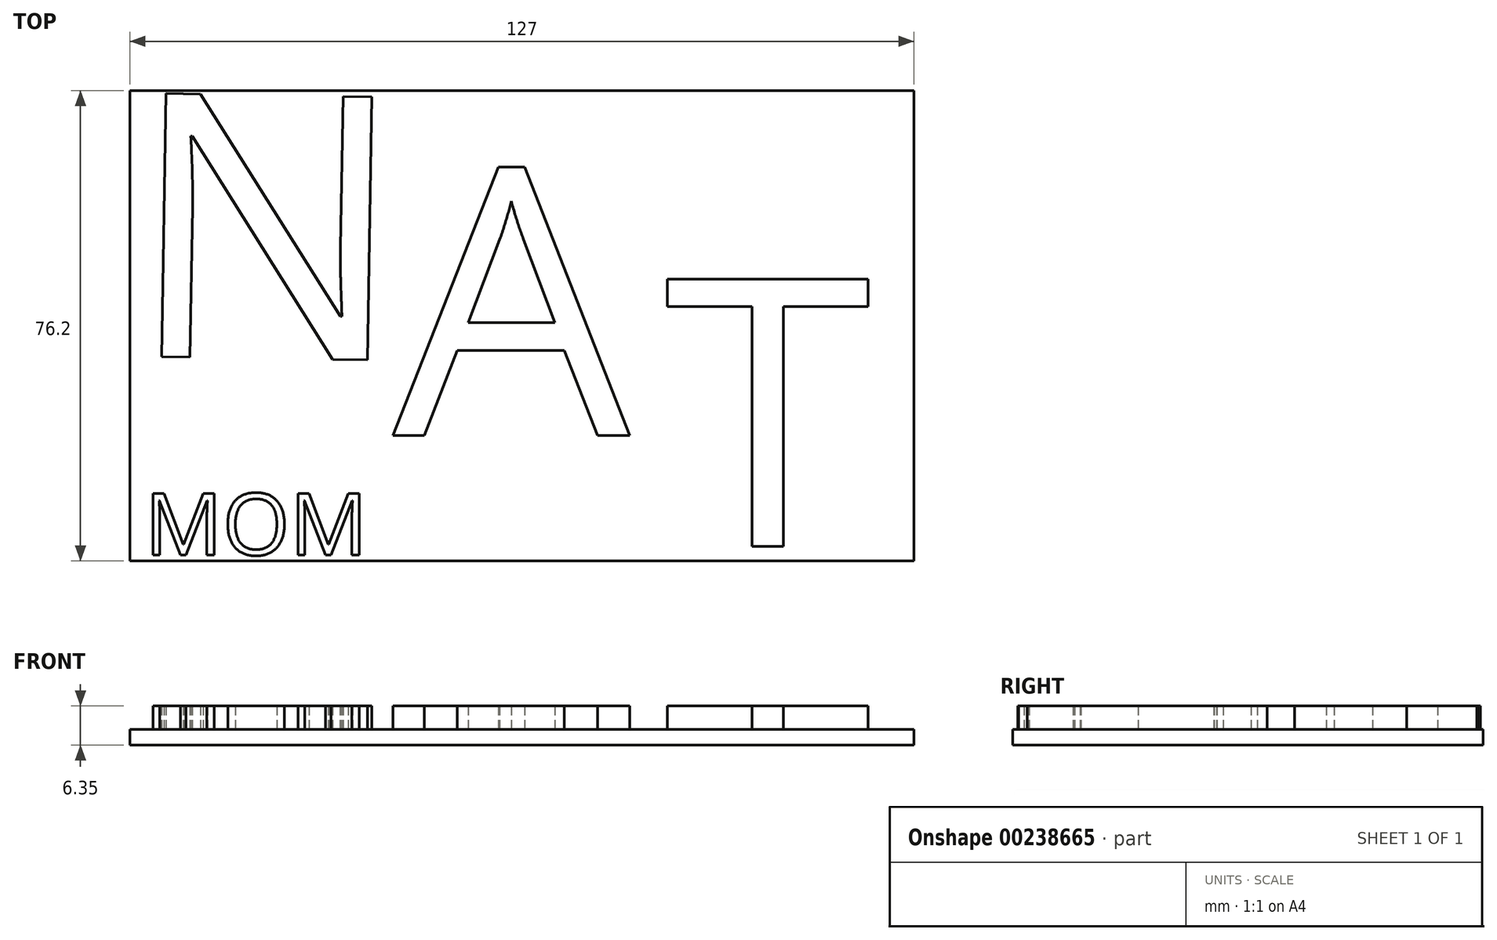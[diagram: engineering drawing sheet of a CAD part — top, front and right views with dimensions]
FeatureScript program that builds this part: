
annotation { "Feature Type Name" : "Feature", "Feature Type Description" : "" }
export const myFeature = defineFeature(function(context is Context, id is Id, definition is map)
    precondition{}
    {
        {
            var Q0;
            Q0=qCreatedBy(makeId("Top.planeOp"),FACE);
            var sketch = newSketch(context, id + "F0", { "sketchPlane" : qUnion([Q0])});
            skLineSegment(sketch, "E0.bottom", {"start": v(0, 0) * mm, "end": v(127, 0) * mm});
            skLineSegment(sketch, "E0.top", {"start": v(0, 76.2) * mm, "end": v(127, 76.2) * mm});
            skLineSegment(sketch, "E0.left", {"start": v(0, 0) * mm, "end": v(0, 76.2) * mm});
            skLineSegment(sketch, "E0.right", {"start": v(127, 0) * mm, "end": v(127, 76.2) * mm});
            skSolve(sketch);
        }
        {
            var Q0;
            Q0 = qSketchRegion(id + "F0", true);
            extrude(context, id + "F1", {"entities" : qUnion([Q0]), "depth" : 2.54 * mm});
        }
        {
            var Q0;
            Q0=makeQuery(id+"F1.opExtrude","CAP_FACE",FACE,{"disambiguationData":[OSD([sQuery(id+"F0.wireOp",EDGE,"E0.bottom"),sQuery(id+"F0.wireOp",EDGE,"E0.top"),sQuery(id+"F0.wireOp",EDGE,"E0.left"),sQuery(id+"F0.wireOp",EDGE,"E0.right")])],"isStart":false});
            var sketch = newSketch(context, id + "F2", { "sketchPlane" : qUnion([Q0])});
            skLineSegment(sketch, "E1", {"start": v(42.33, 76.2) * mm, "end": v(42.33, 0) * mm});
            skLineSegment(sketch, "E2", {"start": v(84.67, 76.2) * mm, "end": v(84.67, 0) * mm});
            skText(sketch, "E3", { "text": "N", "fontName": "OpenSans-Regular.ttf"});
            skText(sketch, "E4", { "text": "A", "fontName": "OpenSans-Regular.ttf"});
            skText(sketch, "E5", { "text": "T", "fontName": "OpenSans-Regular.ttf"});
            const initialGuessF2  = {"E3": [-0.0007, 0.0332, 0.99987, -0.0162, 0.043], "E4": [0.04259, 0.02032, 1, 0, 0.04369], "E5": [0.08655, 0.00235, 1, 0, 0.04369]};
            skSetInitialGuess(sketch, initialGuessF2);
            skSolve(sketch);
        }
        {
            var Q0;
            Q0 = qSketchRegion(id + "F2", true);
            extrude(context, id + "F3", {"entities" : qUnion([Q0]), "operationType" : NewBodyOperationType.ADD, "depth" : 3.8 * mm});
        }
        {
            var Q0;
            {var subQ0=sQuery(id+"F0.wireOp",EDGE,"E0.left");var subQ1=sQuery(id+"F0.wireOp",EDGE,"E0.bottom");var subQ2=sQuery(id+"F0.wireOp",EDGE,"E0.right");var subQ3=sQuery(id+"F0.wireOp",EDGE,"E0.top");Q0=makeQuery(id+"F3.boolean.opBoolean","SPLIT",FACE,{"disambiguationData":[TD([makeQuery(id+"F1.opExtrude","SWEPT_FACE",FACE,{"disambiguationData":[OSD([subQ1])]})])],"derivedFrom":makeQuery(id+"F1.opExtrude","CAP_FACE",FACE,{"disambiguationData":[OSD([subQ1,subQ3,subQ0,subQ2])],"isStart":false})});}
            var sketch = newSketch(context, id + "F4", { "sketchPlane" : qUnion([Q0])});
            skText(sketch, "E6", { "text": "MOM", "fontName": "OpenSans-Regular.ttf"});
            const initialGuessF4  = {"E6": [0.00238, 0.00094, 1, 0, 0.01006]};
            skSetInitialGuess(sketch, initialGuessF4);
            skSolve(sketch);
        }
        {
            var Q0;
            Q0 = qSketchRegion(id + "F4", true);
            extrude(context, id + "F5", {"entities" : qUnion([Q0]), "operationType" : NewBodyOperationType.ADD, "depth" : 3.8 * mm});
        }
    });
